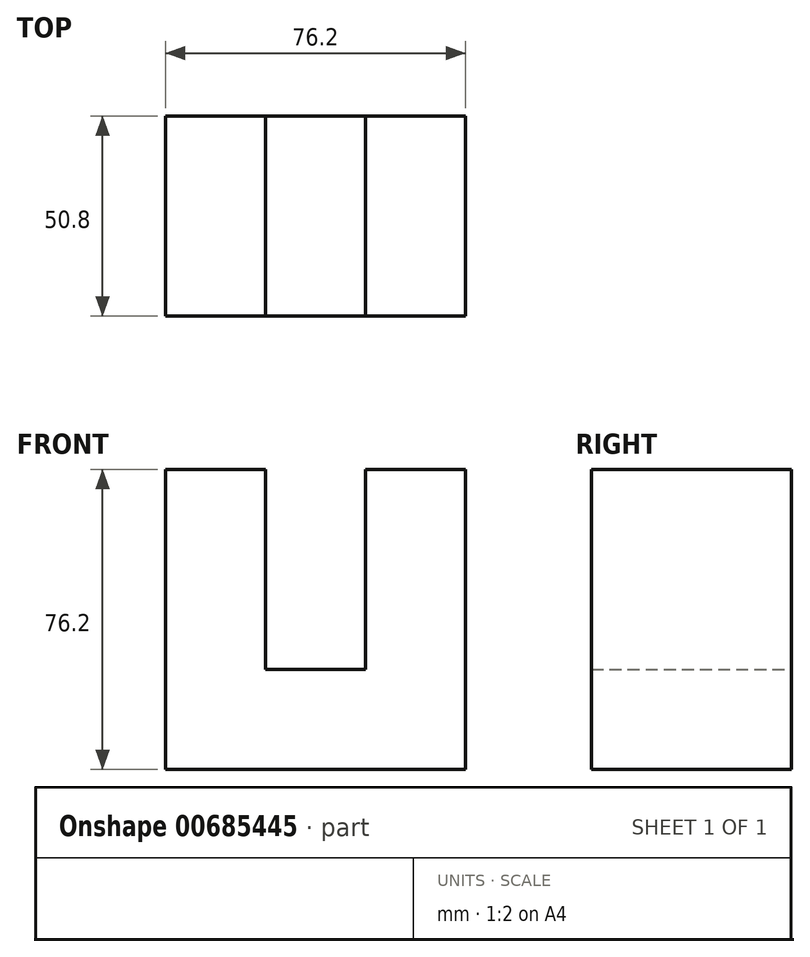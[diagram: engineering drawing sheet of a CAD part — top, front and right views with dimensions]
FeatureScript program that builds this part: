
annotation { "Feature Type Name" : "Feature", "Feature Type Description" : "" }
export const myFeature = defineFeature(function(context is Context, id is Id, definition is map)
    precondition{}
    {
        {
            var Q0;
            Q0=qCreatedBy(makeId("Front.planeOp"),FACE);
            var sketch = newSketch(context, id + "F0", { "sketchPlane" : qUnion([Q0])});
            skLineSegment(sketch, "E0", {"start": v(-50.8, 60.73) * mm, "end": v(-50.8, -15.47) * mm});
            skLineSegment(sketch, "E1", {"start": v(-50.8, 60.73) * mm, "end": v(-25.4, 60.73) * mm});
            skLineSegment(sketch, "E2", {"start": v(-25.4, 60.73) * mm, "end": v(-25.4, 9.93) * mm});
            skLineSegment(sketch, "E3", {"start": v(-25.4, 9.93) * mm, "end": v(0, 9.93) * mm});
            skLineSegment(sketch, "E4", {"start": v(0, 9.93) * mm, "end": v(0, 60.73) * mm});
            skLineSegment(sketch, "E5", {"start": v(0, 60.73) * mm, "end": v(25.4, 60.73) * mm});
            skLineSegment(sketch, "E6", {"start": v(25.4, 60.73) * mm, "end": v(25.4, -15.47) * mm});
            skLineSegment(sketch, "E7", {"start": v(25.4, -15.47) * mm, "end": v(-50.8, -15.47) * mm});
            skSolve(sketch);
        }
        {
            var Q0;
            Q0=makeQuery(id+"F0.imprint","IMPRINT",FACE,{"disambiguationData":[TD([[makeQuery(id+"F0.imprint","IMPRINT",EDGE,{"derivedFrom":sQuery(id+"F0.wireOp",EDGE,"E0")}),1.0]])]});
            extrude(context, id + "F1", {"entities" : qUnion([Q0]), "depth" : 50.8 * mm, "offsetDistance" : 25.4 * mm});
        }
    });
